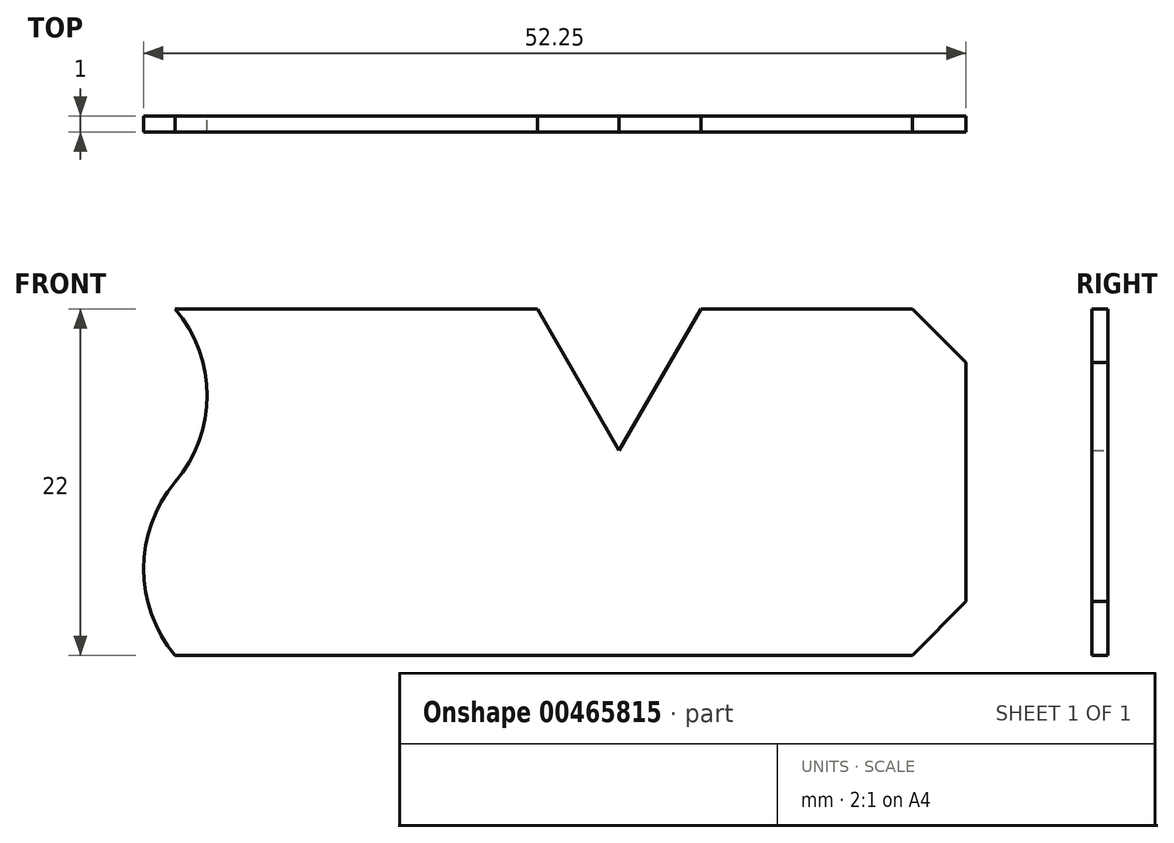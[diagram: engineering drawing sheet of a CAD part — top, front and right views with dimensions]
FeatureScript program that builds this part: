
annotation { "Feature Type Name" : "Feature", "Feature Type Description" : "" }
export const myFeature = defineFeature(function(context is Context, id is Id, definition is map)
    precondition{}
    {
        {
            var Q0;
            Q0=qCreatedBy(makeId("Front.planeOp"),FACE);
            var sketch = newSketch(context, id + "F0", { "sketchPlane" : qUnion([Q0])});
            skLineSegment(sketch, "E0", {"start": v(90.17, 36.97) * mm, "end": v(113.17, 36.97) * mm});
            skLineSegment(sketch, "E1", {"start": v(113.17, 36.97) * mm, "end": v(118.37, 27.97) * mm});
            skLineSegment(sketch, "E2", {"start": v(118.37, 27.97) * mm, "end": v(123.57, 36.97) * mm});
            skLineSegment(sketch, "E3", {"start": v(123.57, 36.97) * mm, "end": v(137, 36.97) * mm});
            skLineSegment(sketch, "E4", {"start": v(137, 36.97) * mm, "end": v(140.4, 33.56) * mm});
            skArc(sketch, "E5", {"start": v(90.17, 25.97) * mm, "mid": v(92.2, 31.47) * mm, "end": v(90.17, 36.97) * mm});
            skLineSegment(sketch, "E6", {"start": v(83.7, 31.47) * mm, "end": v(96.64, 20.47) * mm, "construction": true});
            skArc(sketch, "E7", {"start": v(90.17, 25.97) * mm, "mid": v(88.15, 20.47) * mm, "end": v(90.17, 14.97) * mm});
            skLineSegment(sketch, "E8", {"start": v(74.79, 36.97) * mm, "end": v(74.79, 14.97) * mm, "construction": true});
            skPoint(sketch, "E9", {"position": v(74.79, 25.97) * mm});
            skPoint(sketch, "E10", {"position": v(90.17, 25.97) * mm});
            skLineSegment(sketch, "E11", {"start": v(90.17, 14.97) * mm, "end": v(111.17, 14.97) * mm});
            skLineSegment(sketch, "E12", {"start": v(111.17, 14.97) * mm, "end": v(116.37, 23.97) * mm, "construction": true});
            skLineSegment(sketch, "E13", {"start": v(116.37, 23.97) * mm, "end": v(121.57, 14.97) * mm});
            skLineSegment(sketch, "E14", {"start": v(113.17, 53.7) * mm, "end": v(123.57, 53.7) * mm, "construction": true});
            skPoint(sketch, "E15", {"position": v(118.37, 53.7) * mm});
            skLineSegment(sketch, "E16", {"start": v(140.4, 33.56) * mm, "end": v(140.4, 25.97) * mm});
            skLineSegment(sketch, "E17", {"start": v(69.18, 25.97) * mm, "end": v(55.9, 25.97) * mm, "construction": true});
            skLineSegment(sketch, "E18.MirrorCS", {"start": v(140.4, 18.38) * mm, "end": v(140.4, 25.97) * mm});
            skLineSegment(sketch, "E19.MirrorCS", {"start": v(137, 14.97) * mm, "end": v(140.4, 18.38) * mm});
            skLineSegment(sketch, "E20", {"start": v(121.57, 14.97) * mm, "end": v(137, 14.97) * mm});
            skLineSegment(sketch, "E21", {"start": v(111.17, 14.97) * mm, "end": v(121.57, 14.97) * mm});
            skSolve(sketch);
        }
        {
            var Q0;
            Q0=makeQuery(id+"F0.imprint","IMPRINT",FACE,{"disambiguationData":[TD([[makeQuery(id+"F0.imprint","IMPRINT",EDGE,{"derivedFrom":sQuery(id+"F0.wireOp",EDGE,"E0")}),-1.0]])]});
            extrude(context, id + "F1", {"entities" : qUnion([Q0]), "depth" : 1 * mm});
        }
    });
